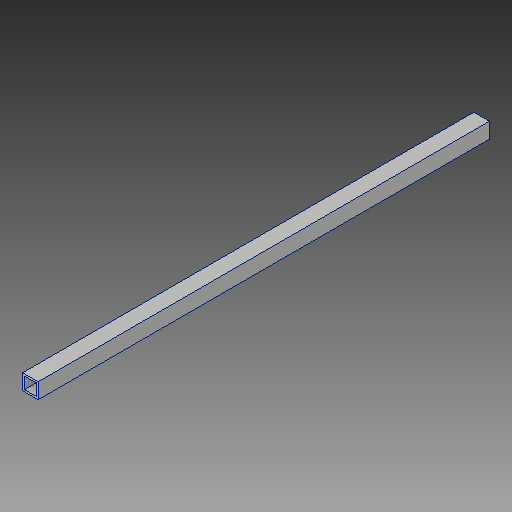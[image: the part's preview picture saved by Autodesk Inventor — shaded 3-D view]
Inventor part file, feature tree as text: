
AUTODESK INVENTOR PART (.ipt)
format: ipt  version: 2018 (Build 220112000, 112)  size: 113,152 bytes
history: native  units: in
note: dims shown in document units (in); Inventor stores cm internally (conversion verified against a paired STEP export)
features: extrude x3, sketch x3
ambient origin geometry x8: Origin, YZ Plane, XZ Plane, XY Plane, X Axis, Y Axis, Z Axis, Center Point
bodies: Solid1 (feature_tree)
feature tree (6):
  extrude  "Extrusion1"  Depth=1.0in
  extrude  "Extrusion2"  Depth=0.125in
  extrude  "Extrusion3"  Depth=0.75in
  sketch  "Sketch1"  dims[d0=31.0in d1=1.0in]
  sketch  "Sketch2"  dims[d2=1.0in d3=0.0in d4=0.125in]
  sketch  "Sketch3"  dims[d5=0.125in d6=0.75in d7=0.75in d8=31.0in d9=0.0in d10=2.0in d11=0.0in]
